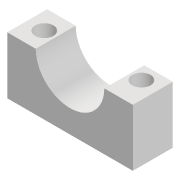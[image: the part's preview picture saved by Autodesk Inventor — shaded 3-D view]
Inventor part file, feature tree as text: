
AUTODESK INVENTOR PART (.ipt)
format: ipt  version: 2022 (Build 260153000, 153)  size: 108,032 bytes
history: native  units: mm
features: extrude x2, sketch x2
ambient origin geometry x8: Origin, YZ Plane, XZ Plane, XY Plane, X Axis, Y Axis, Z Axis, Center Point
bodies: Solid1 (feature_tree)
feature tree (4):
  extrude  "Extrusion1"  Depth=11.0mm
  extrude  "Extrusion2"  Depth=10.0mm
  sketch  "Sketch2"  dims[d0=12.0mm d1=11.0mm]
  sketch  "Sketch3"  dims[d2=11.0mm d3=10.0mm d4=3.0mm d5=7.0mm d6=0.0mm d7=3.2mm d8=3.0mm d9=3.5mm d10=3.2mm d11=3.0mm d12=3.5mm d13=10.0mm d14=0.0mm]
